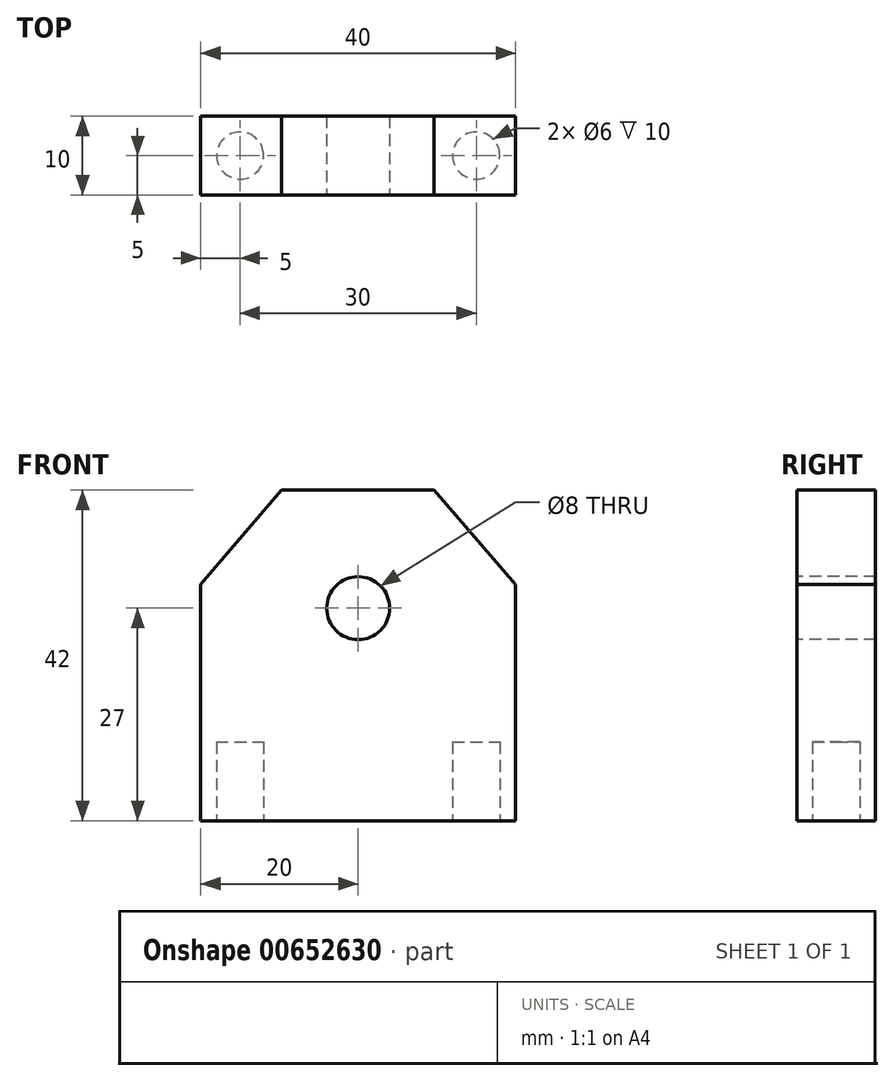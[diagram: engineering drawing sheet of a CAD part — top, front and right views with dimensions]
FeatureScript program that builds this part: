
annotation { "Feature Type Name" : "Feature", "Feature Type Description" : "" }
export const myFeature = defineFeature(function(context is Context, id is Id, definition is map)
    precondition{}
    {
        {
            var Q0;
            Q0=qCreatedBy(makeId("Front.planeOp"),FACE);
            var sketch = newSketch(context, id + "F0", { "sketchPlane" : qUnion([Q0])});
            skLineSegment(sketch, "E0", {"start": v(-20, 0) * mm, "end": v(20, 0) * mm});
            skLineSegment(sketch, "E1", {"start": v(20, 0) * mm, "end": v(20, 30) * mm});
            skLineSegment(sketch, "E2", {"start": v(20, 30) * mm, "end": v(9.61, 42) * mm});
            skLineSegment(sketch, "E3", {"start": v(9.61, 42) * mm, "end": v(-9.72, 42) * mm});
            skLineSegment(sketch, "E4", {"start": v(-9.72, 42) * mm, "end": v(-20, 30) * mm});
            skLineSegment(sketch, "E5", {"start": v(-20, 30) * mm, "end": v(-20, 0) * mm});
            skCircle(sketch, "E6", {"center": v(0, 27) * mm, "radius": 4 * mm});
            skSolve(sketch);
        }
        {
            var Q0;
            Q0=qSketchRegion(id+"F0",true);
            extrude(context, id + "F1", {"entities" : qUnion([Q0]), "oppositeDirection" : true, "depth" : 10 * mm, "offsetDistance" : 25 * mm});
        }
        {
            var Q0;
            Q0=makeQuery(id+"F1.opExtrude","SWEPT_FACE",FACE,{"disambiguationData":[OSD([sQuery(id+"F0.wireOp",EDGE,"E0")])]});
            var sketch = newSketch(context, id + "F2", { "sketchPlane" : qUnion([Q0])});
            skCircle(sketch, "E7", {"center": v(-15, -5) * mm, "radius": 3 * mm});
            skCircle(sketch, "E8", {"center": v(15, -5) * mm, "radius": 3 * mm});
            skSolve(sketch);
        }
        {
            var Q0;
            Q0=makeQuery(id+"F2.imprint","IMPRINT",FACE,{"disambiguationData":[TD([[makeQuery(id+"F2.imprint","IMPRINT",EDGE,{"derivedFrom":sQuery(id+"F2.wireOp",EDGE,"E7")}),1.0]])]});
            var Q1;
            Q1=makeQuery(id+"F2.imprint","IMPRINT",FACE,{"disambiguationData":[TD([[makeQuery(id+"F2.imprint","IMPRINT",EDGE,{"derivedFrom":sQuery(id+"F2.wireOp",EDGE,"E8")}),1.0]])]});
            extrude(context, id + "F3", {"entities" : qUnion([Q0, Q1]), "operationType" : NewBodyOperationType.REMOVE, "oppositeDirection" : true, "depth" : 10 * mm, "offsetDistance" : 25 * mm});
        }
    });
